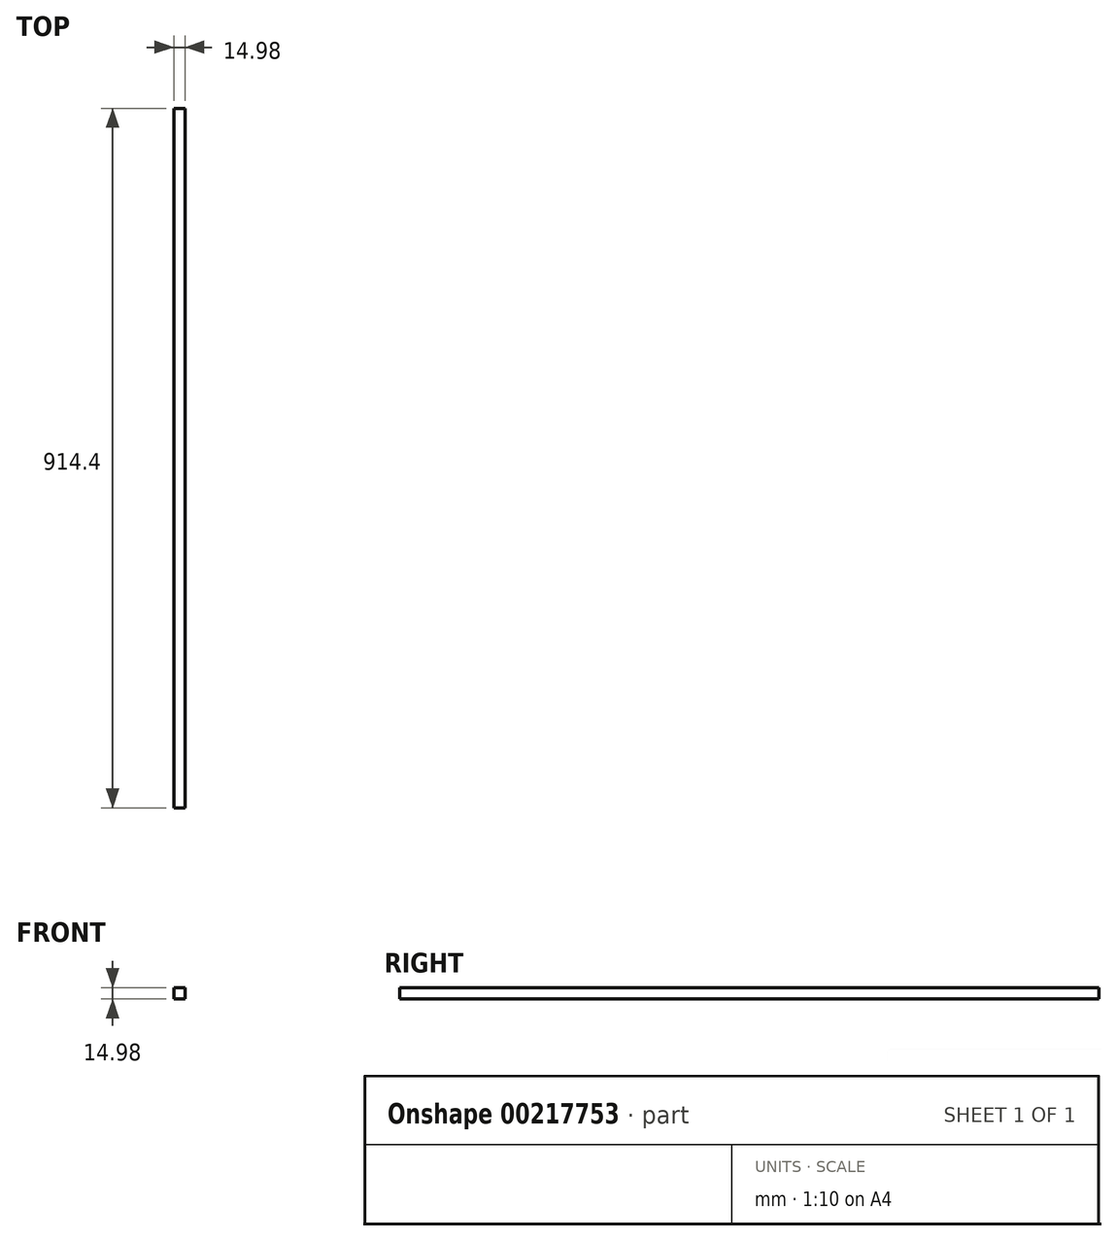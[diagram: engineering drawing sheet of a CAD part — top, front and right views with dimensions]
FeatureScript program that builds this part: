
annotation { "Feature Type Name" : "Feature", "Feature Type Description" : "" }
export const myFeature = defineFeature(function(context is Context, id is Id, definition is map)
    precondition{}
    {
        {
            var Q0;
            Q0=qCreatedBy(makeId("Front.planeOp"),FACE);
            var sketch = newSketch(context, id + "F0", { "sketchPlane" : qUnion([Q0])});
            skLineSegment(sketch, "E0.bottom", {"start": v(7.5, 7.5) * mm, "end": v(-7.5, 7.5) * mm});
            skLineSegment(sketch, "E0.top", {"start": v(7.5, -7.5) * mm, "end": v(-7.5, -7.5) * mm});
            skLineSegment(sketch, "E0.left", {"start": v(7.5, 7.5) * mm, "end": v(7.5, -7.5) * mm});
            skLineSegment(sketch, "E0.right", {"start": v(-7.5, 7.5) * mm, "end": v(-7.5, -7.5) * mm});
            skPoint(sketch, "E0.middle", {"position": v(0, 0) * mm});
            skSolve(sketch);
        }
        {
            var Q0;
            Q0 = qSketchRegion(id + "F0", true);
            extrude(context, id + "F1", {"entities" : qUnion([Q0]), "depth" : 914.4 * mm});
        }
    });
